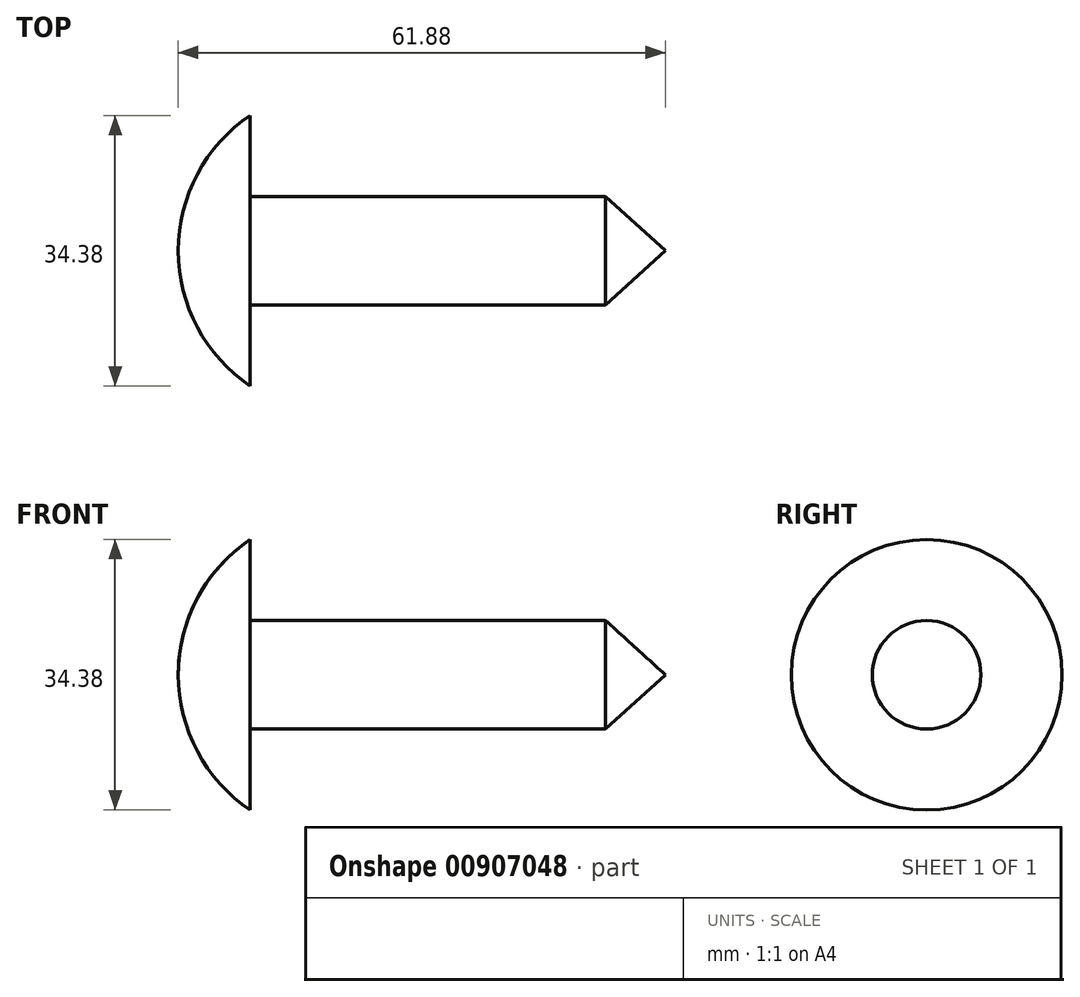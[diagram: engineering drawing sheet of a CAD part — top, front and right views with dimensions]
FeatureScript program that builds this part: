
annotation { "Feature Type Name" : "Feature", "Feature Type Description" : "" }
export const myFeature = defineFeature(function(context is Context, id is Id, definition is map)
    precondition{}
    {
        {
            var Q0;
            Q0=qCreatedBy(makeId("Front.planeOp"),FACE);
            var sketch = newSketch(context, id + "F0", { "sketchPlane" : qUnion([Q0])});
            skLineSegment(sketch, "E0", {"start": v(0, 17.19) * mm, "end": v(0, 6.9) * mm});
            skLineSegment(sketch, "E1", {"start": v(0, 6.9) * mm, "end": v(45.15, 6.9) * mm});
            skLineSegment(sketch, "E2", {"start": v(45.15, 6.9) * mm, "end": v(52.73, 0) * mm});
            skArc(sketch, "E3", {"start": v(0, 17.19) * mm, "mid": v(-6.72, 9.74) * mm, "end": v(-9.15, 0) * mm});
            skLineSegment(sketch, "E4", {"start": v(-9.15, 0) * mm, "end": v(52.73, 0) * mm});
            skSolve(sketch);
        }
        {
            var Q0;
            Q0=makeQuery(id+"F0.imprint","IMPRINT",FACE,{"disambiguationData":[TD([[makeQuery(id+"F0.imprint","IMPRINT",EDGE,{"derivedFrom":sQuery(id+"F0.wireOp",EDGE,"E0")}),-1.0]])]});
            var Q1;
            Q1=sQuery(id+"F0.wireOp",EDGE,"E4");
            revolve(context, id + "F1", {"surfaceOperationType" : NewSurfaceOperationType.NEW, "entities" : qUnion([Q0]), "axis" : qUnion([Q1]), "revolveType" : RevolveType.FULL});
        }
    });
